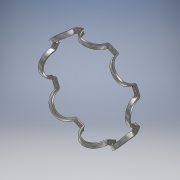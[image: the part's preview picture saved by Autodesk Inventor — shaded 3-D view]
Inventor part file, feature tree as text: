
AUTODESK INVENTOR PART (.ipt)
format: ipt  version: 2018 (Build 220112000, 112)  size: 327,680 bytes
history: native  units: mm
features: sketch x3, extrude x2, pattern_circular x2, revolve x1, fillet x1, shell x1
ambient origin geometry x8: Origin, YZ Plane, XZ Plane, XY Plane, X Axis, Y Axis, Z Axis, Center Point
bodies: Solid1 (feature_tree)
feature tree (10):
  extrude  "Extrusion1"  Depth=86.0mm
  revolve  "Revolution1"  [1 undecoded]
  fillet  "Fillet1"  Radius=24.0mm
  pattern_circular  "Circular Pattern1"  Angle=90.0deg  [1 undecoded]
  shell  "Shell1"  Thickness=2.1mm
  extrude  "Extrusion2"  Depth=1.5mm TaperAngle=360.0deg
  pattern_circular  "Circular Pattern2"  [2 undecoded]
  sketch  "Sketch1"  dims[d0=94.0mm d1=86.0mm]
  sketch  "Sketch2"  dims[d2=16.0mm d3=0.0mm d4=90.0mm d5=24.0mm]
  sketch  "Sketch3"  dims[d6=24.0mm d7=90.0deg d8=2.1mm d9=80.0mm d10=360.0deg d12=1.5mm d13=90.0mm d14=22.5deg d15=2.0mm d16=16.0mm d17=0.0mm d18=80.0mm d19=360.0deg]
note: 4 required parameter values undecoded (feature->parameter linkage not recoverable at this tier; creation-order binding heuristic only, values carry confidence <= 0.55)